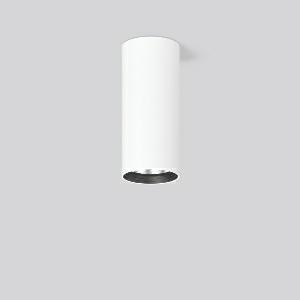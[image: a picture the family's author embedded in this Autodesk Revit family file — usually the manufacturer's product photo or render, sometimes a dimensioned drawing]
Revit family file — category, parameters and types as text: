
# Revit family: heledon_mini_a_931209_002_1_3204
name_source: partatom
category: Lighting Fixtures
units: mm (PartAtom-declared; Revit-internal decimal feet)

## family parameters
Cut with Voids When Loaded = No
Host = Face
Light Source = No
Part Type = Normal
Room Calculation Point = No
Round Connector Dimension = Use Diameter
Shared = No

## types (1)
- HELEDON mini A (1 x LED Modul 940, 3700 lm, 4000)
    Apparent Load = 29 VA
    Approval mark = CE
    CIE Flux Codes = 99 100 100 100 100
    Color Rendering = 92
    Color Temperature = 4000
    Default Elevation = 1800 mm
    Description = Series: HELEDON mini
Cylindrical surface-mounted downlight. Housing: die-cast aluminium, powder-coated. Internal ceiling frame polycarbonate with bayonet mounting. Black plastic ring and recessed LED to prevent glare from the side. Optical assembly with reflector made of MIRO-Silver with 98% total light reflection for outstanding efficiency - can be changed without tools. Best colour rendering index Ra>90. Suitable for Ceiling mounting. Easy installation with a separate ceiling frame with bayonet mounting and plug connection. Driver integrated. Connected via plug-in connector. High quality converter without flickering and stroboscopic effect. The following accessories can be mounted without use of tools: interchangeable lenses, decorative glasses, honeycomb louvre, clear and frosted diffusers, white interchangeable plastic ring. 
Colour: traffic white, matt (RAL 9016)
Diameter: 87 mm
Height: 197 mm
Lamp: LED
Socket: without socket
Colour temperature: 4000K
Colour rendering index (CRI): 92
System power: 29 W
Rated luminous flux: 3700 lm
Luminous efficiency: 128 lm/W
Control gear: Regulated power supply
Protection class: I
Type of protection: IP 20
    Height = 197 mm
    Lamp = 1 x LED Modul 940
    Lamp Light Flux = 3700 lm
    Lamp count = 1
    Length = 87 mm
    Lifetime = 50000 h
    Luminous efficacy = 128 lm/W
    Manufacturer = RZB
    ModVariant = No
    Model = 931209.002.1
    Mounting Place = Ceiling
    Mounting Type = Surface mounted
    Number of Poles = 1
    OnlyDefault = Yes
    Power Factor = 1
    Product Name = HELEDON mini A
    Product group = Surface mounted downlights
    ProductGroupID = 302
    Protection Class = Protection class I
    Protection Degree = IP 20
    RLX_Detail_Level = 1
    RLX_Emergency_Light_Flux = 0 lm
    RLX_Emergency_Type = 0
    RLX_Emergency_Type_DB = No
    RlxData = <blob elided: 107505 chars, md5=cba3a32f>
    Socket = socket
    Standby Power = 0 W
    System Light Flux = 3700 lm
    System Power = 29 W
    Type Comments = Product without accessories
    Type Image = 931188.002.jpg
    URL = http://relux.com
    VarID = ---
    Voltage = 230 V
    Voltage Range = 220-240 V
    Weight = 0.00 kg
    Width = 0 mm  [stored 0 ft]

note: [stored X ft] marks values corroborated as IEEE doubles in the binary element streams (Revit-internal decimal feet)

## geometry (parser evidence)
native form markers: Blend x4, Sweep x9
no freeform markers — native parametric forms only
